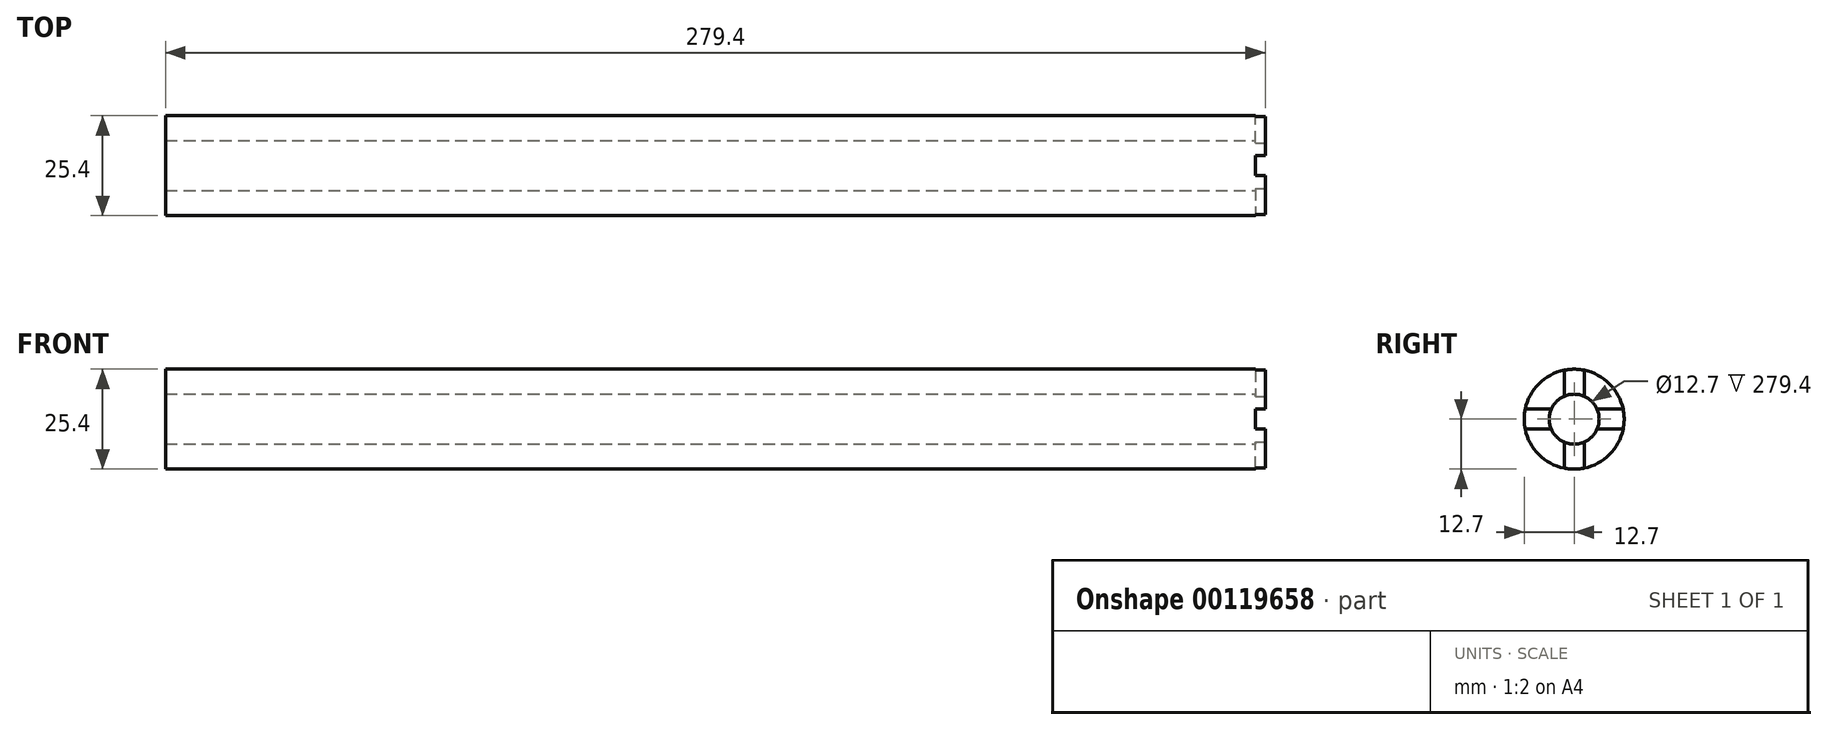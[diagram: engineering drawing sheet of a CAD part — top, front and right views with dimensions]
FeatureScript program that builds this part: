
annotation { "Feature Type Name" : "Feature", "Feature Type Description" : "" }
export const myFeature = defineFeature(function(context is Context, id is Id, definition is map)
    precondition{}
    {
        {
            var Q0;
            Q0=qCreatedBy(makeId("Front.planeOp"),FACE);
            var sketch = newSketch(context, id + "F0", { "sketchPlane" : qUnion([Q0])});
            skLineSegment(sketch, "E0", {"start": v(0, 0) * mm, "end": v(0, 12.7) * mm});
            skLineSegment(sketch, "E1", {"start": v(0, 12.7) * mm, "end": v(52.45, 12.7) * mm});
            skLineSegment(sketch, "E2", {"start": v(52.45, 12.7) * mm, "end": v(52.45, 0) * mm});
            skLineSegment(sketch, "E3", {"start": v(52.45, 0) * mm, "end": v(0, 0) * mm});
            skLineSegment(sketch, "E4", {"start": v(52.45, 12.7) * mm, "end": v(279.4, 12.7) * mm});
            skLineSegment(sketch, "E5", {"start": v(279.4, 12.7) * mm, "end": v(279.4, 0) * mm});
            skLineSegment(sketch, "E6", {"start": v(279.4, 0) * mm, "end": v(52.45, 0) * mm});
            skLineSegment(sketch, "E7", {"start": v(260.35, 0) * mm, "end": v(260.35, 12.7) * mm});
            skSolve(sketch);
        }
        {
            var Q0;
            Q0 = qSketchRegion(id + "F0", true);
            var Q1;
            Q1=sQuery(id+"F0.wireOp",EDGE,"E3");
            revolve(context, id + "F1", {"entities" : qUnion([Q0]), "axis" : qUnion([Q1]), "revolveType" : RevolveType.FULL});
        }
        {
            var Q0;
            Q0=makeQuery(id+"F1.opRevolve","SWEPT_FACE",FACE,{"disambiguationData":[OSD([sQuery(id+"F0.wireOp",EDGE,"E5")])]});
            var sketch = newSketch(context, id + "F2", { "sketchPlane" : qUnion([Q0])});
            skCircle(sketch, "E8", {"center": v(0, 0) * mm, "radius": 12.7 * mm});
            skCircle(sketch, "E9", {"center": v(0, 0) * mm, "radius": 6.35 * mm});
            skLineSegment(sketch, "E10", {"start": v(2.54, 12.44) * mm, "end": v(2.54, 5.82) * mm});
            skLineSegment(sketch, "E11", {"start": v(-2.54, 12.44) * mm, "end": v(-2.54, 5.82) * mm});
            skArc(sketch, "E12", {"start": v(2.54, 12.44) * mm, "mid": v(0, 12.7) * mm, "end": v(-2.54, 12.44) * mm});
            skLineSegment(sketch, "E13", {"start": v(0, 0) * mm, "end": v(0, 12.7) * mm, "construction": true});
            skPoint(sketch, "E14.positionSnap0", {"position": v(0, 12.7) * mm});
            skLineSegment(sketch, "E15", {"start": v(0, 0) * mm, "end": v(0, -12.7) * mm, "construction": true});
            skLineSegment(sketch, "E16", {"start": v(-12.7, 0) * mm, "end": v(12.7, 0) * mm, "construction": true});
            skLineSegment(sketch, "E17.MirrorCS", {"start": v(2.54, -12.44) * mm, "end": v(2.54, -5.82) * mm});
            skLineSegment(sketch, "E18.MirrorCS", {"start": v(-2.54, -12.44) * mm, "end": v(-2.54, -5.82) * mm});
            skArc(sketch, "E19.MirrorCS", {"start": v(2.54, -12.44) * mm, "mid": v(0, -12.7) * mm, "end": v(-2.54, -12.44) * mm});
            skLineSegment(sketch, "E20", {"start": v(5.82, 2.54) * mm, "end": v(12.44, 2.54) * mm});
            skLineSegment(sketch, "E21", {"start": v(5.82, -2.54) * mm, "end": v(12.44, -2.54) * mm});
            skArc(sketch, "E22", {"start": v(12.44, -2.54) * mm, "mid": v(12.7, 0) * mm, "end": v(12.44, 2.54) * mm});
            skPoint(sketch, "E23", {"position": v(12.7, 0) * mm});
            skLineSegment(sketch, "E24.MirrorCS", {"start": v(-5.82, 2.54) * mm, "end": v(-12.44, 2.54) * mm});
            skLineSegment(sketch, "E25.MirrorCS", {"start": v(-5.82, -2.54) * mm, "end": v(-12.44, -2.54) * mm});
            skPoint(sketch, "E26.MirrorP", {"position": v(-12.7, 0) * mm});
            skSolve(sketch);
        }
        {
            var Q0;
            {var subQ0=sQuery(id+"F2.wireOp",EDGE,"E10");Q0=makeQuery(id+"F2.imprint","IMPRINT",FACE,{"disambiguationData":[TD([[makeQuery(id+"F2.imprint","IMPRINT",EDGE,{"derivedFrom":subQ0}),-1.0]])]});}
            var Q1;
            {var subQ0=sQuery(id+"F2.wireOp",EDGE,"E24.MirrorCS");Q1=makeQuery(id+"F2.imprint","IMPRINT",FACE,{"disambiguationData":[TD([[makeQuery(id+"F2.imprint","IMPRINT",EDGE,{"derivedFrom":subQ0}),1.0]])]});}
            var Q2;
            {var subQ0=sQuery(id+"F2.wireOp",EDGE,"E20");Q2=makeQuery(id+"F2.imprint","IMPRINT",FACE,{"disambiguationData":[TD([[makeQuery(id+"F2.imprint","IMPRINT",EDGE,{"derivedFrom":subQ0}),-1.0]])]});}
            var Q3;
            {var subQ0=sQuery(id+"F2.wireOp",EDGE,"E17.MirrorCS");Q3=makeQuery(id+"F2.imprint","IMPRINT",FACE,{"disambiguationData":[TD([[makeQuery(id+"F2.imprint","IMPRINT",EDGE,{"derivedFrom":subQ0}),1.0]])]});}
            extrude(context, id + "F3", {"entities" : qUnion([Q0, Q1, Q2, Q3]), "operationType" : NewBodyOperationType.REMOVE, "oppositeDirection" : true, "depth" : 2.54 * mm});
        }
        {
            var Q0;
            {var subQ0=sQuery(id+"F2.wireOp",EDGE,"E9");var subQ4=makeQuery(id+"F2.imprint","INTERSECT",VERTEX,{"derivedFrom":[subQ0,sQuery(id+"F2.wireOp",EDGE,"E10")]});Q0=makeQuery(id+"F2.imprint","IMPRINT",FACE,{"disambiguationData":[TD([[makeQuery(id+"F2.imprint","IMPRINT",EDGE,{"disambiguationData":[TD([[subQ4,1.0]])],"derivedFrom":subQ0}),1.0]])]});}
            extrude(context, id + "F4", {"entities" : qUnion([Q0]), "operationType" : NewBodyOperationType.REMOVE, "endBound" : BoundingType.THROUGH_ALL, "oppositeDirection" : true, "depth" : 25.4 * mm});
        }
    });
